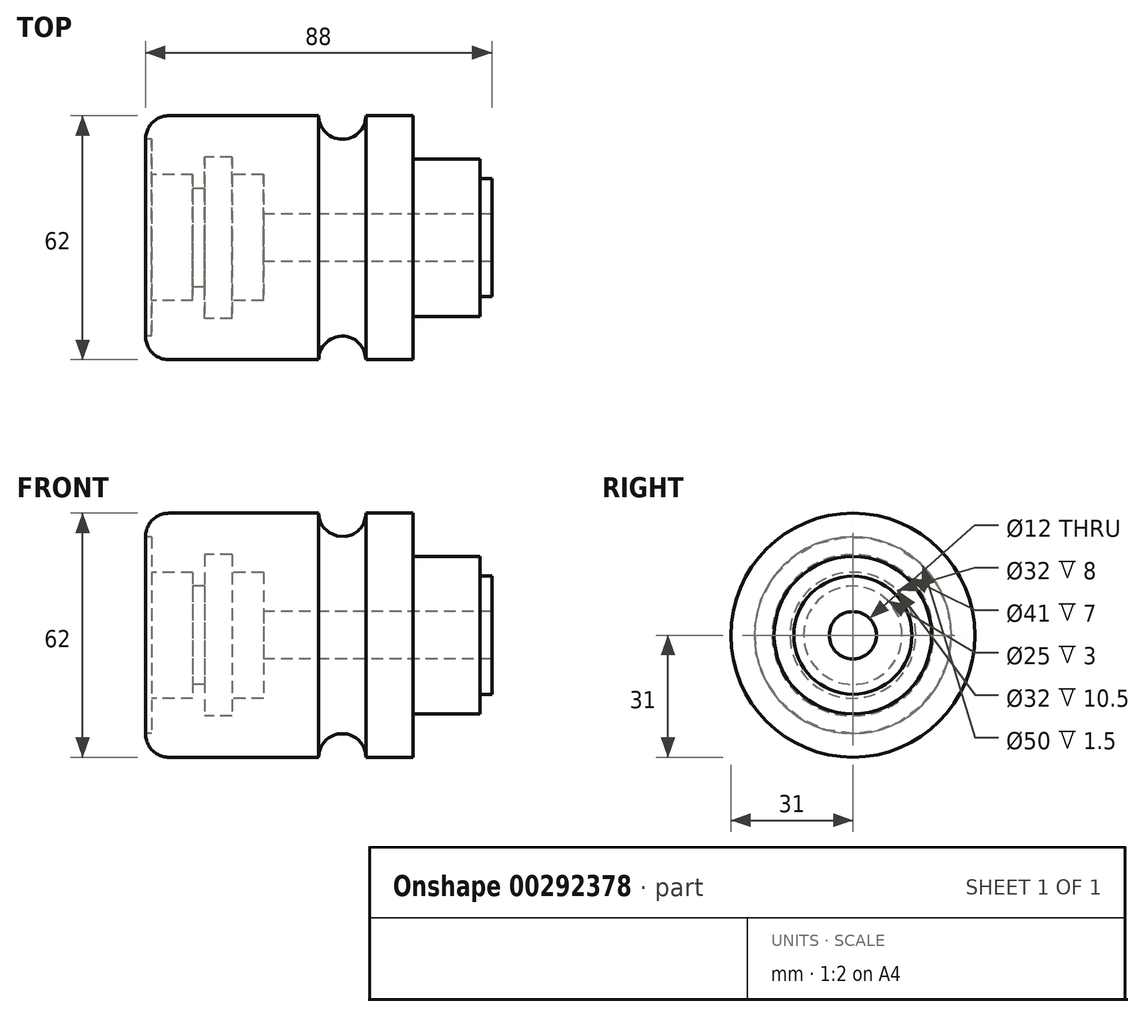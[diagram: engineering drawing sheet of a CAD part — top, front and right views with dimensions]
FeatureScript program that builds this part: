
annotation { "Feature Type Name" : "Feature", "Feature Type Description" : "" }
export const myFeature = defineFeature(function(context is Context, id is Id, definition is map)
    precondition{}
    {
        {
            var Q0;
            Q0=qCreatedBy(makeId("Front.planeOp"),FACE);
            var sketch = newSketch(context, id + "F0", { "sketchPlane" : qUnion([Q0])});
            skLineSegment(sketch, "E0", {"start": v(0, 0) * mm, "end": v(0, 31) * mm});
            skLineSegment(sketch, "E1", {"start": v(68, 31) * mm, "end": v(68, 20) * mm});
            skLineSegment(sketch, "E2", {"start": v(68, 20) * mm, "end": v(85, 20) * mm});
            skLineSegment(sketch, "E3", {"start": v(85, 20) * mm, "end": v(85, 15) * mm});
            skLineSegment(sketch, "E4", {"start": v(85, 15) * mm, "end": v(88, 15) * mm});
            skLineSegment(sketch, "E5", {"start": v(88, 15) * mm, "end": v(88, 0) * mm});
            skLineSegment(sketch, "E6", {"start": v(88, 0) * mm, "end": v(0, 0) * mm});
            skLineSegment(sketch, "E7", {"start": v(0, 0) * mm, "end": v(69.3, 0) * mm, "construction": true});
            skLineSegment(sketch, "E8", {"start": v(0, 31) * mm, "end": v(44, 31) * mm});
            skArc(sketch, "E9", {"start": v(44, 31) * mm, "mid": v(50, 25) * mm, "end": v(56, 31) * mm});
            skLineSegment(sketch, "E10.trimOffspring", {"start": v(56, 31) * mm, "end": v(68, 31) * mm});
            skSolve(sketch);
        }
        {
            var Q0;
            Q0=makeQuery(id+"F0.imprint","IMPRINT",FACE,{"disambiguationData":[TD([[makeQuery(id+"F0.imprint","IMPRINT",EDGE,{"derivedFrom":sQuery(id+"F0.wireOp",EDGE,"E0")}),-1.0]])]});
            var Q1;
            Q1=sQuery(id+"F0.wireOp",EDGE,"E6");
            revolve(context, id + "F1", {"entities" : qUnion([Q0]), "axis" : qUnion([Q1]), "revolveType" : RevolveType.FULL});
        }
        {
            var Q0;
            Q0=qCreatedBy(makeId("Front.planeOp"),FACE);
            var sketch = newSketch(context, id + "F2", { "sketchPlane" : qUnion([Q0])});
            skLineSegment(sketch, "E11", {"start": v(0, 0) * mm, "end": v(0, 25) * mm});
            skLineSegment(sketch, "E12", {"start": v(0, 25) * mm, "end": v(1.5, 25) * mm});
            skLineSegment(sketch, "E13", {"start": v(1.5, 25) * mm, "end": v(1.5, 16) * mm});
            skLineSegment(sketch, "E14", {"start": v(1.5, 16) * mm, "end": v(12, 16) * mm});
            skLineSegment(sketch, "E15", {"start": v(12, 16) * mm, "end": v(12, 12.5) * mm});
            skLineSegment(sketch, "E16", {"start": v(12, 12.5) * mm, "end": v(15, 12.5) * mm});
            skLineSegment(sketch, "E17", {"start": v(15, 12.5) * mm, "end": v(15, 20.5) * mm});
            skLineSegment(sketch, "E18", {"start": v(15, 20.5) * mm, "end": v(22, 20.5) * mm});
            skLineSegment(sketch, "E19", {"start": v(22, 20.5) * mm, "end": v(22, 16) * mm});
            skLineSegment(sketch, "E20", {"start": v(22, 16) * mm, "end": v(30, 16) * mm});
            skLineSegment(sketch, "E21", {"start": v(30, 16) * mm, "end": v(30, 6) * mm});
            skLineSegment(sketch, "E22", {"start": v(30, 6) * mm, "end": v(88, 6) * mm});
            skLineSegment(sketch, "E23", {"start": v(88, 6) * mm, "end": v(88, 0) * mm});
            skLineSegment(sketch, "E24", {"start": v(88, 0) * mm, "end": v(-28.04, 0) * mm, "construction": true});
            skLineSegment(sketch, "E25", {"start": v(0, 0) * mm, "end": v(88, 0) * mm});
            skSolve(sketch);
        }
        {
            var Q0;
            Q0 = qSketchRegion(id + "F2", true);
            var Q1;
            Q1=sQuery(id+"F2.wireOp",EDGE,"E24");
            revolve(context, id + "F3", {"operationType" : NewBodyOperationType.REMOVE, "entities" : qUnion([Q0]), "axis" : qUnion([Q1]), "revolveType" : RevolveType.FULL, "oppositeDirection" : true});
        }
        {
            var Q0;
            Q0=makeQuery(id+"F1.opRevolve","SWEPT_EDGE",EDGE,{"disambiguationData":[OSD([sQuery(id+"F0.wireOp",EDGE,"E0"),sQuery(id+"F0.wireOp",EDGE,"E8")])]});
            fillet(context, id + "F4", {"entities" : qUnion([Q0]), "radius" : 6 * mm, "tangentPropagation" : true, "allowEdgeOverflow" : false});
        }
    });
